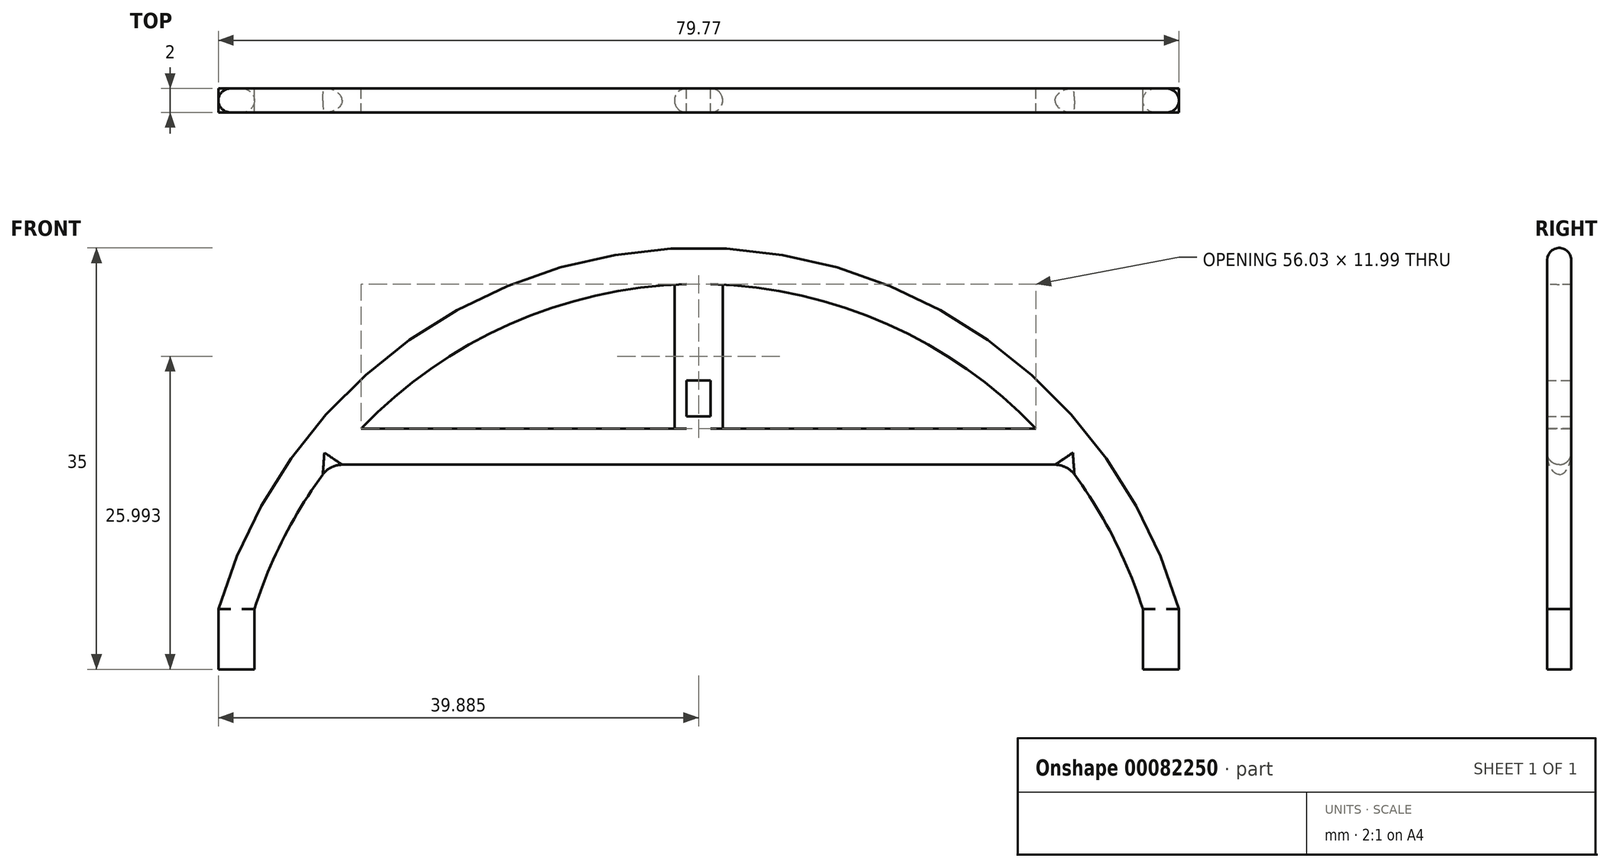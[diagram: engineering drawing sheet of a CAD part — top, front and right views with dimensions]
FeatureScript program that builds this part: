
annotation { "Feature Type Name" : "Feature", "Feature Type Description" : "" }
export const myFeature = defineFeature(function(context is Context, id is Id, definition is map)
    precondition{}
    {
        {
            var Q0;
            Q0=qCreatedBy(makeId("Front.planeOp"),FACE);
            var sketch = newSketch(context, id + "F0", { "sketchPlane" : qUnion([Q0])});
            skArc(sketch, "E0", {"start": v(34.32, -19.8) * mm, "mid": v(-5.57, 10.2) * mm, "end": v(-45.45, -19.8) * mm});
            skArc(sketch, "E1", {"start": v(31.32, -19.8) * mm, "mid": v(-5.57, 7.2) * mm, "end": v(-42.45, -19.8) * mm});
            skLineSegment(sketch, "E2", {"start": v(-45.45, -19.8) * mm, "end": v(-42.45, -19.8) * mm});
            skLineSegment(sketch, "E3", {"start": v(31.32, -19.8) * mm, "end": v(34.32, -19.8) * mm});
            skPoint(sketch, "E4.endSnap0", {"position": v(-5.57, 7.2) * mm});
            skLineSegment(sketch, "E5", {"start": v(-36.16, -7.8) * mm, "end": v(25.03, -7.8) * mm});
            skPoint(sketch, "E6.startSnap0", {"position": v(-5.57, -7.8) * mm});
            skLineSegment(sketch, "E7", {"start": v(-33.58, -4.8) * mm, "end": v(22.45, -4.8) * mm});
            skLineSegment(sketch, "E8", {"start": v(-7.57, 0.2) * mm, "end": v(-7.57, -4.8) * mm});
            skLineSegment(sketch, "E9", {"start": v(-3.57, 0.2) * mm, "end": v(-3.57, -4.8) * mm});
            skLineSegment(sketch, "E10", {"start": v(-6.57, -0.8) * mm, "end": v(-6.57, -3.8) * mm});
            skLineSegment(sketch, "E11", {"start": v(-6.57, -0.8) * mm, "end": v(-4.57, -0.8) * mm});
            skLineSegment(sketch, "E12", {"start": v(-4.57, -0.8) * mm, "end": v(-4.57, -3.8) * mm});
            skLineSegment(sketch, "E13", {"start": v(-4.57, -3.8) * mm, "end": v(-6.57, -3.8) * mm});
            skLineSegment(sketch, "E14", {"start": v(-7.57, 0.2) * mm, "end": v(-7.57, 7.15) * mm});
            skLineSegment(sketch, "E15", {"start": v(-3.57, 0.2) * mm, "end": v(-3.57, 7.15) * mm});
            skSolve(sketch);
        }
        {
            var Q0;
            Q0=makeQuery(id+"F0.imprint","IMPRINT",FACE,{"disambiguationData":[TD([[makeQuery(id+"F0.imprint","IMPRINT",EDGE,{"derivedFrom":sQuery(id+"F0.wireOp",EDGE,"E0")}),1.0]])]});
            var Q1;
            Q1=makeQuery(id+"F0.imprint","IMPRINT",FACE,{"disambiguationData":[TD([[makeQuery(id+"F0.imprint","IMPRINT",EDGE,{"derivedFrom":sQuery(id+"F0.wireOp",EDGE,"QaKfyl1q-dLBN-I6Pb-Zep1-DZlAWYqTSGp9")}),1.0]])]});
            var Q2;
            Q2=makeQuery(id+"F0.imprint","IMPRINT",FACE,{"disambiguationData":[TD([[makeQuery(id+"F0.imprint","IMPRINT",EDGE,{"derivedFrom":sQuery(id+"F0.wireOp",EDGE,"O7wW7FGu-E0O4-MFLM-AW0a-nUHi2M2s85NZ")}),-1.0]])]});
            var Q3;
            {var subQ0=sQuery(id+"F0.wireOp",EDGE,"E5");Q3=makeQuery(id+"F0.imprint","IMPRINT",FACE,{"disambiguationData":[TD([[makeQuery(id+"F0.imprint","IMPRINT",EDGE,{"derivedFrom":subQ0}),1.0]])]});}
            var Q4;
            {var subQ1=sQuery(id+"F0.wireOp",EDGE,"E8");Q4=makeQuery(id+"F0.imprint","IMPRINT",FACE,{"disambiguationData":[TD([[makeQuery(id+"F0.imprint","IMPRINT",EDGE,{"derivedFrom":subQ1}),1.0]])]});}
            extrude(context, id + "F1", {"entities" : qUnion([Q0, Q1, Q2, Q3, Q4]), "depth" : 2 * mm});
        }
        {
            var Q0;
            Q0=makeQuery(id+"F1.opExtrude","SWEPT_FACE",FACE,{"disambiguationData":[OSD([sQuery(id+"F0.wireOp",EDGE,"E3")])]});
            var sketch = newSketch(context, id + "F2", { "sketchPlane" : qUnion([Q0])});
            skLineSegment(sketch, "E16", {"start": v(31.32, 2) * mm, "end": v(31.32, 0) * mm});
            skLineSegment(sketch, "E17", {"start": v(31.32, 0) * mm, "end": v(34.32, 0) * mm});
            skLineSegment(sketch, "E18", {"start": v(34.32, 0) * mm, "end": v(34.32, 2) * mm});
            skLineSegment(sketch, "E19", {"start": v(34.32, 2) * mm, "end": v(31.32, 2) * mm});
            skSolve(sketch);
        }
        {
            var Q0;
            Q0=makeQuery(id+"F1.opExtrude","SWEPT_FACE",FACE,{"disambiguationData":[OSD([sQuery(id+"F0.wireOp",EDGE,"E2")])]});
            var sketch = newSketch(context, id + "F3", { "sketchPlane" : qUnion([Q0])});
            skLineSegment(sketch, "E20", {"start": v(-45.45, 2) * mm, "end": v(-45.45, 0) * mm});
            skLineSegment(sketch, "E21", {"start": v(-45.45, 0) * mm, "end": v(-42.45, 0) * mm});
            skLineSegment(sketch, "E22", {"start": v(-42.45, 0) * mm, "end": v(-42.45, 2) * mm});
            skLineSegment(sketch, "E23", {"start": v(-42.45, 2) * mm, "end": v(-45.45, 2) * mm});
            skSolve(sketch);
        }
        {
            var Q0;
            Q0=makeQuery(id+"F1.opExtrude","CAP_EDGE",EDGE,{"disambiguationData":[OSD([sQuery(id+"F0.wireOp",EDGE,"E0")])],"isStart":false});
            var Q1;
            {var subQ0=sQuery(id+"F0.wireOp",EDGE,"E1");Q1=makeQuery(id+"F1.opExtrude","CAP_EDGE",EDGE,{"disambiguationData":[OSD([subQ0]),TDD([makeQuery(id+"F0.imprint","IMPRINT",EDGE,{"disambiguationData":[TD([[makeQuery(id+"F0.imprint","INTERSECT",VERTEX,{"disambiguationData":[OD(0.0)],"derivedFrom":[subQ0,sQuery(id+"F0.wireOp",EDGE,"E7")]}),1.0]])],"derivedFrom":subQ0})])],"isStart":false});}
            var Q2;
            {var subQ0=sQuery(id+"F0.wireOp",EDGE,"E7");Q2=makeQuery(id+"F1.opExtrude","CAP_EDGE",EDGE,{"disambiguationData":[OSD([subQ0]),TDD([makeQuery(id+"F0.imprint","IMPRINT",EDGE,{"disambiguationData":[TD([[makeQuery(id+"F0.imprint","INTERSECT",VERTEX,{"disambiguationData":[OD(0.0)],"derivedFrom":[sQuery(id+"F0.wireOp",EDGE,"E1"),subQ0]}),-1.0]])],"derivedFrom":subQ0})])],"isStart":false});}
            var Q3;
            Q3=makeQuery(id+"F1.opExtrude","CAP_EDGE",EDGE,{"disambiguationData":[OSD([sQuery(id+"F0.wireOp",EDGE,"E8"),sQuery(id+"F0.wireOp",EDGE,"E14")])],"isStart":false});
            var Q4;
            Q4=makeQuery(id+"F1.opExtrude","CAP_EDGE",EDGE,{"disambiguationData":[OSD([sQuery(id+"F0.wireOp",EDGE,"E9"),sQuery(id+"F0.wireOp",EDGE,"E15")])],"isStart":false});
            var Q5;
            {var subQ0=sQuery(id+"F0.wireOp",EDGE,"E1");Q5=makeQuery(id+"F1.opExtrude","CAP_EDGE",EDGE,{"disambiguationData":[OSD([subQ0]),TDD([makeQuery(id+"F0.imprint","IMPRINT",EDGE,{"disambiguationData":[TD([[makeQuery(id+"F0.imprint","INTERSECT",VERTEX,{"disambiguationData":[OD(1.0)],"derivedFrom":[subQ0,sQuery(id+"F0.wireOp",EDGE,"E7")]}),-1.0]])],"derivedFrom":subQ0})])],"isStart":false});}
            var Q6;
            {var subQ0=sQuery(id+"F0.wireOp",EDGE,"E7");Q6=makeQuery(id+"F1.opExtrude","CAP_EDGE",EDGE,{"disambiguationData":[OSD([subQ0]),TDD([makeQuery(id+"F0.imprint","IMPRINT",EDGE,{"disambiguationData":[TD([[makeQuery(id+"F0.imprint","INTERSECT",VERTEX,{"disambiguationData":[OD(1.0)],"derivedFrom":[sQuery(id+"F0.wireOp",EDGE,"E1"),subQ0]}),1.0]])],"derivedFrom":subQ0})])],"isStart":false});}
            var Q7;
            Q7=makeQuery(id+"F1.opExtrude","CAP_EDGE",EDGE,{"disambiguationData":[OSD([sQuery(id+"F0.wireOp",EDGE,"E0")])],"isStart":true});
            var Q8;
            {var subQ0=sQuery(id+"F0.wireOp",EDGE,"E7");Q8=makeQuery(id+"F1.opExtrude","CAP_EDGE",EDGE,{"disambiguationData":[OSD([subQ0]),TDD([makeQuery(id+"F0.imprint","IMPRINT",EDGE,{"disambiguationData":[TD([[makeQuery(id+"F0.imprint","INTERSECT",VERTEX,{"disambiguationData":[OD(1.0)],"derivedFrom":[sQuery(id+"F0.wireOp",EDGE,"E1"),subQ0]}),1.0]])],"derivedFrom":subQ0})])],"isStart":true});}
            var Q9;
            {var subQ0=sQuery(id+"F0.wireOp",EDGE,"E1");Q9=makeQuery(id+"F1.opExtrude","CAP_EDGE",EDGE,{"disambiguationData":[OSD([subQ0]),TDD([makeQuery(id+"F0.imprint","IMPRINT",EDGE,{"disambiguationData":[TD([[makeQuery(id+"F0.imprint","INTERSECT",VERTEX,{"disambiguationData":[OD(1.0)],"derivedFrom":[subQ0,sQuery(id+"F0.wireOp",EDGE,"E7")]}),-1.0]])],"derivedFrom":subQ0})])],"isStart":true});}
            var Q10;
            Q10=makeQuery(id+"F1.opExtrude","CAP_EDGE",EDGE,{"disambiguationData":[OSD([sQuery(id+"F0.wireOp",EDGE,"E9"),sQuery(id+"F0.wireOp",EDGE,"E15")])],"isStart":true});
            var Q11;
            {var subQ0=sQuery(id+"F0.wireOp",EDGE,"E1");Q11=makeQuery(id+"F1.opExtrude","CAP_EDGE",EDGE,{"disambiguationData":[OSD([subQ0]),TDD([makeQuery(id+"F0.imprint","IMPRINT",EDGE,{"disambiguationData":[TD([[makeQuery(id+"F0.imprint","INTERSECT",VERTEX,{"disambiguationData":[OD(0.0)],"derivedFrom":[subQ0,sQuery(id+"F0.wireOp",EDGE,"E7")]}),1.0]])],"derivedFrom":subQ0})])],"isStart":true});}
            var Q12;
            Q12=makeQuery(id+"F1.opExtrude","CAP_EDGE",EDGE,{"disambiguationData":[OSD([sQuery(id+"F0.wireOp",EDGE,"E8"),sQuery(id+"F0.wireOp",EDGE,"E14")])],"isStart":true});
            var Q13;
            {var subQ0=sQuery(id+"F0.wireOp",EDGE,"E7");Q13=makeQuery(id+"F1.opExtrude","CAP_EDGE",EDGE,{"disambiguationData":[OSD([subQ0]),TDD([makeQuery(id+"F0.imprint","IMPRINT",EDGE,{"disambiguationData":[TD([[makeQuery(id+"F0.imprint","INTERSECT",VERTEX,{"disambiguationData":[OD(0.0)],"derivedFrom":[sQuery(id+"F0.wireOp",EDGE,"E1"),subQ0]}),-1.0]])],"derivedFrom":subQ0})])],"isStart":true});}
            var Q14;
            {var subQ0=sQuery(id+"F0.wireOp",EDGE,"E1");Q14=makeQuery(id+"F1.opExtrude","CAP_EDGE",EDGE,{"disambiguationData":[OSD([subQ0]),TDD([makeQuery(id+"F0.imprint","IMPRINT",EDGE,{"disambiguationData":[TD([[makeQuery(id+"F0.imprint","INTERSECT",VERTEX,{"disambiguationData":[OD(0.0)],"derivedFrom":[subQ0,sQuery(id+"F0.wireOp",EDGE,"E5")]}),-1.0]])],"derivedFrom":subQ0})])],"isStart":true});}
            var Q15;
            {var subQ0=sQuery(id+"F0.wireOp",EDGE,"E1");Q15=makeQuery(id+"F1.opExtrude","CAP_EDGE",EDGE,{"disambiguationData":[OSD([subQ0]),TDD([makeQuery(id+"F0.imprint","IMPRINT",EDGE,{"disambiguationData":[TD([[makeQuery(id+"F0.imprint","INTERSECT",VERTEX,{"disambiguationData":[OD(1.0)],"derivedFrom":[subQ0,sQuery(id+"F0.wireOp",EDGE,"E5")]}),1.0]])],"derivedFrom":subQ0})])],"isStart":true});}
            var Q16;
            Q16=makeQuery(id+"F1.opExtrude","CAP_EDGE",EDGE,{"disambiguationData":[OSD([sQuery(id+"F0.wireOp",EDGE,"E5")])],"isStart":true});
            var Q17;
            {var subQ0=sQuery(id+"F0.wireOp",EDGE,"E1");Q17=makeQuery(id+"F1.opExtrude","CAP_EDGE",EDGE,{"disambiguationData":[OSD([subQ0]),TDD([makeQuery(id+"F0.imprint","IMPRINT",EDGE,{"disambiguationData":[TD([[makeQuery(id+"F0.imprint","INTERSECT",VERTEX,{"disambiguationData":[OD(0.0)],"derivedFrom":[subQ0,sQuery(id+"F0.wireOp",EDGE,"E5")]}),-1.0]])],"derivedFrom":subQ0})])],"isStart":false});}
            var Q18;
            Q18=makeQuery(id+"F1.opExtrude","CAP_EDGE",EDGE,{"disambiguationData":[OSD([sQuery(id+"F0.wireOp",EDGE,"E5")])],"isStart":false});
            var Q19;
            {var subQ0=sQuery(id+"F0.wireOp",EDGE,"E1");Q19=makeQuery(id+"F1.opExtrude","CAP_EDGE",EDGE,{"disambiguationData":[OSD([subQ0]),TDD([makeQuery(id+"F0.imprint","IMPRINT",EDGE,{"disambiguationData":[TD([[makeQuery(id+"F0.imprint","INTERSECT",VERTEX,{"disambiguationData":[OD(1.0)],"derivedFrom":[subQ0,sQuery(id+"F0.wireOp",EDGE,"E5")]}),1.0]])],"derivedFrom":subQ0})])],"isStart":false});}
            fillet(context, id + "F4", {"entities" : qUnion([Q0, Q1, Q2, Q3, Q4, Q5, Q6, Q7, Q8, Q9, Q10, Q11, Q12, Q13, Q14, Q15, Q16, Q17, Q18, Q19]), "radius" : 1 * mm, "tangentPropagation" : true, "allowEdgeOverflow" : false});
        }
        {
            var Q0;
            {var subQ0=sQuery(id+"F0.wireOp",EDGE,"E7");var subQ1=sQuery(id+"F0.wireOp",EDGE,"E1");var subQ2=makeQuery(id+"F0.imprint","INTERSECT",VERTEX,{"disambiguationData":[OD(0.0)],"derivedFrom":[subQ1,subQ0]});Q0=makeQuery(id+"F4.opFillet","BLEND_EDGE",EDGE,{"blendedFrom":[makeQuery(id+"F1.opExtrude","CAP_EDGE",EDGE,{"disambiguationData":[OSD([subQ1]),TDD([makeQuery(id+"F0.imprint","IMPRINT",EDGE,{"disambiguationData":[TD([[subQ2,1.0]])],"derivedFrom":subQ1})])],"isStart":false}),makeQuery(id+"F1.opExtrude","CAP_EDGE",EDGE,{"disambiguationData":[OSD([subQ0]),TDD([makeQuery(id+"F0.imprint","IMPRINT",EDGE,{"disambiguationData":[TD([[subQ2,-1.0]])],"derivedFrom":subQ0})])],"isStart":false})],"blendedInto":[]});}
            var Q1;
            {var subQ0=sQuery(id+"F0.wireOp",EDGE,"E7");var subQ1=sQuery(id+"F0.wireOp",EDGE,"E1");var subQ2=makeQuery(id+"F0.imprint","INTERSECT",VERTEX,{"disambiguationData":[OD(0.0)],"derivedFrom":[subQ1,subQ0]});Q1=makeQuery(id+"F4.opFillet","BLEND_EDGE",EDGE,{"blendedFrom":[makeQuery(id+"F1.opExtrude","CAP_EDGE",EDGE,{"disambiguationData":[OSD([subQ1]),TDD([makeQuery(id+"F0.imprint","IMPRINT",EDGE,{"disambiguationData":[TD([[subQ2,1.0]])],"derivedFrom":subQ1})])],"isStart":true}),makeQuery(id+"F1.opExtrude","CAP_EDGE",EDGE,{"disambiguationData":[OSD([subQ0]),TDD([makeQuery(id+"F0.imprint","IMPRINT",EDGE,{"disambiguationData":[TD([[subQ2,-1.0]])],"derivedFrom":subQ0})])],"isStart":true})],"blendedInto":[]});}
            var Q2;
            {var subQ0=sQuery(id+"F0.wireOp",EDGE,"E7");var subQ1=sQuery(id+"F0.wireOp",EDGE,"E1");var subQ2=makeQuery(id+"F0.imprint","INTERSECT",VERTEX,{"disambiguationData":[OD(1.0)],"derivedFrom":[subQ1,subQ0]});Q2=makeQuery(id+"F4.opFillet","BLEND_EDGE",EDGE,{"blendedFrom":[makeQuery(id+"F1.opExtrude","CAP_EDGE",EDGE,{"disambiguationData":[OSD([subQ1]),TDD([makeQuery(id+"F0.imprint","IMPRINT",EDGE,{"disambiguationData":[TD([[subQ2,-1.0]])],"derivedFrom":subQ1})])],"isStart":true}),makeQuery(id+"F1.opExtrude","CAP_EDGE",EDGE,{"disambiguationData":[OSD([subQ0]),TDD([makeQuery(id+"F0.imprint","IMPRINT",EDGE,{"disambiguationData":[TD([[subQ2,1.0]])],"derivedFrom":subQ0})])],"isStart":true})],"blendedInto":[]});}
            var Q3;
            {var subQ0=sQuery(id+"F0.wireOp",EDGE,"E7");var subQ1=sQuery(id+"F0.wireOp",EDGE,"E1");var subQ2=makeQuery(id+"F0.imprint","INTERSECT",VERTEX,{"disambiguationData":[OD(1.0)],"derivedFrom":[subQ1,subQ0]});Q3=makeQuery(id+"F4.opFillet","BLEND_EDGE",EDGE,{"blendedFrom":[makeQuery(id+"F1.opExtrude","CAP_EDGE",EDGE,{"disambiguationData":[OSD([subQ1]),TDD([makeQuery(id+"F0.imprint","IMPRINT",EDGE,{"disambiguationData":[TD([[subQ2,-1.0]])],"derivedFrom":subQ1})])],"isStart":false}),makeQuery(id+"F1.opExtrude","CAP_EDGE",EDGE,{"disambiguationData":[OSD([subQ0]),TDD([makeQuery(id+"F0.imprint","IMPRINT",EDGE,{"disambiguationData":[TD([[subQ2,1.0]])],"derivedFrom":subQ0})])],"isStart":false})],"blendedInto":[]});}
            var Q4;
            {var subQ0=sQuery(id+"F0.wireOp",EDGE,"E8");var subQ1=sQuery(id+"F0.wireOp",EDGE,"E7");Q4=makeQuery(id+"F4.opFillet","BLEND_EDGE",EDGE,{"blendedFrom":[makeQuery(id+"F1.opExtrude","CAP_EDGE",EDGE,{"disambiguationData":[OSD([subQ1]),TDD([makeQuery(id+"F0.imprint","IMPRINT",EDGE,{"disambiguationData":[TD([[makeQuery(id+"F0.imprint","INTERSECT",VERTEX,{"disambiguationData":[OD(0.0)],"derivedFrom":[sQuery(id+"F0.wireOp",EDGE,"E1"),subQ1]}),-1.0]])],"derivedFrom":subQ1})])],"isStart":false}),makeQuery(id+"F1.opExtrude","CAP_EDGE",EDGE,{"disambiguationData":[OSD([subQ0,sQuery(id+"F0.wireOp",EDGE,"E14")])],"isStart":false})],"blendedInto":[]});}
            var Q5;
            {var subQ0=sQuery(id+"F0.wireOp",EDGE,"E9");var subQ1=sQuery(id+"F0.wireOp",EDGE,"E7");Q5=makeQuery(id+"F4.opFillet","BLEND_EDGE",EDGE,{"blendedFrom":[makeQuery(id+"F1.opExtrude","CAP_EDGE",EDGE,{"disambiguationData":[OSD([subQ1]),TDD([makeQuery(id+"F0.imprint","IMPRINT",EDGE,{"disambiguationData":[TD([[makeQuery(id+"F0.imprint","INTERSECT",VERTEX,{"disambiguationData":[OD(1.0)],"derivedFrom":[sQuery(id+"F0.wireOp",EDGE,"E1"),subQ1]}),1.0]])],"derivedFrom":subQ1})])],"isStart":false}),makeQuery(id+"F1.opExtrude","CAP_EDGE",EDGE,{"disambiguationData":[OSD([subQ0,sQuery(id+"F0.wireOp",EDGE,"E15")])],"isStart":false})],"blendedInto":[]});}
            var Q6;
            {var subQ0=sQuery(id+"F0.wireOp",EDGE,"E15");var subQ1=sQuery(id+"F0.wireOp",EDGE,"E1");Q6=makeQuery(id+"F4.opFillet","BLEND_EDGE",EDGE,{"blendedFrom":[makeQuery(id+"F1.opExtrude","CAP_EDGE",EDGE,{"disambiguationData":[OSD([subQ1]),TDD([makeQuery(id+"F0.imprint","IMPRINT",EDGE,{"disambiguationData":[TD([[makeQuery(id+"F0.imprint","INTERSECT",VERTEX,{"disambiguationData":[OD(1.0)],"derivedFrom":[subQ1,sQuery(id+"F0.wireOp",EDGE,"E7")]}),-1.0]])],"derivedFrom":subQ1})])],"isStart":false}),makeQuery(id+"F1.opExtrude","CAP_EDGE",EDGE,{"disambiguationData":[OSD([sQuery(id+"F0.wireOp",EDGE,"E9"),subQ0])],"isStart":false})],"blendedInto":[]});}
            var Q7;
            {var subQ0=sQuery(id+"F0.wireOp",EDGE,"E15");var subQ1=sQuery(id+"F0.wireOp",EDGE,"E1");Q7=makeQuery(id+"F4.opFillet","BLEND_EDGE",EDGE,{"blendedFrom":[makeQuery(id+"F1.opExtrude","CAP_EDGE",EDGE,{"disambiguationData":[OSD([subQ1]),TDD([makeQuery(id+"F0.imprint","IMPRINT",EDGE,{"disambiguationData":[TD([[makeQuery(id+"F0.imprint","INTERSECT",VERTEX,{"disambiguationData":[OD(1.0)],"derivedFrom":[subQ1,sQuery(id+"F0.wireOp",EDGE,"E7")]}),-1.0]])],"derivedFrom":subQ1})])],"isStart":true}),makeQuery(id+"F1.opExtrude","CAP_EDGE",EDGE,{"disambiguationData":[OSD([sQuery(id+"F0.wireOp",EDGE,"E9"),subQ0])],"isStart":true})],"blendedInto":[]});}
            var Q8;
            {var subQ0=sQuery(id+"F0.wireOp",EDGE,"E14");var subQ1=sQuery(id+"F0.wireOp",EDGE,"E1");Q8=makeQuery(id+"F4.opFillet","BLEND_EDGE",EDGE,{"blendedFrom":[makeQuery(id+"F1.opExtrude","CAP_EDGE",EDGE,{"disambiguationData":[OSD([subQ1]),TDD([makeQuery(id+"F0.imprint","IMPRINT",EDGE,{"disambiguationData":[TD([[makeQuery(id+"F0.imprint","INTERSECT",VERTEX,{"disambiguationData":[OD(0.0)],"derivedFrom":[subQ1,sQuery(id+"F0.wireOp",EDGE,"E7")]}),1.0]])],"derivedFrom":subQ1})])],"isStart":true}),makeQuery(id+"F1.opExtrude","CAP_EDGE",EDGE,{"disambiguationData":[OSD([sQuery(id+"F0.wireOp",EDGE,"E8"),subQ0])],"isStart":true})],"blendedInto":[]});}
            var Q9;
            {var subQ0=sQuery(id+"F0.wireOp",EDGE,"E14");var subQ1=sQuery(id+"F0.wireOp",EDGE,"E1");Q9=makeQuery(id+"F4.opFillet","BLEND_EDGE",EDGE,{"blendedFrom":[makeQuery(id+"F1.opExtrude","CAP_EDGE",EDGE,{"disambiguationData":[OSD([subQ1]),TDD([makeQuery(id+"F0.imprint","IMPRINT",EDGE,{"disambiguationData":[TD([[makeQuery(id+"F0.imprint","INTERSECT",VERTEX,{"disambiguationData":[OD(0.0)],"derivedFrom":[subQ1,sQuery(id+"F0.wireOp",EDGE,"E7")]}),1.0]])],"derivedFrom":subQ1})])],"isStart":false}),makeQuery(id+"F1.opExtrude","CAP_EDGE",EDGE,{"disambiguationData":[OSD([sQuery(id+"F0.wireOp",EDGE,"E8"),subQ0])],"isStart":false})],"blendedInto":[]});}
            var Q10;
            {var subQ0=sQuery(id+"F0.wireOp",EDGE,"E5");var subQ1=sQuery(id+"F0.wireOp",EDGE,"E1");Q10=makeQuery(id+"F4.opFillet","BLEND_EDGE",EDGE,{"blendedFrom":[makeQuery(id+"F1.opExtrude","CAP_EDGE",EDGE,{"disambiguationData":[OSD([subQ1]),TDD([makeQuery(id+"F0.imprint","IMPRINT",EDGE,{"disambiguationData":[TD([[makeQuery(id+"F0.imprint","INTERSECT",VERTEX,{"derivedFrom":[subQ1,sQuery(id+"F0.wireOp",EDGE,"E2")]}),1.0]])],"derivedFrom":subQ1})])],"isStart":false}),makeQuery(id+"F1.opExtrude","CAP_EDGE",EDGE,{"disambiguationData":[OSD([subQ0])],"isStart":false})],"blendedInto":[]});}
            var Q11;
            {var subQ0=sQuery(id+"F0.wireOp",EDGE,"E5");var subQ1=sQuery(id+"F0.wireOp",EDGE,"E1");Q11=makeQuery(id+"F4.opFillet","BLEND_EDGE",EDGE,{"blendedFrom":[makeQuery(id+"F1.opExtrude","CAP_EDGE",EDGE,{"disambiguationData":[OSD([subQ1]),TDD([makeQuery(id+"F0.imprint","IMPRINT",EDGE,{"disambiguationData":[TD([[makeQuery(id+"F0.imprint","INTERSECT",VERTEX,{"derivedFrom":[subQ1,sQuery(id+"F0.wireOp",EDGE,"E2")]}),1.0]])],"derivedFrom":subQ1})])],"isStart":true}),makeQuery(id+"F1.opExtrude","CAP_EDGE",EDGE,{"disambiguationData":[OSD([subQ0])],"isStart":true})],"blendedInto":[]});}
            var Q12;
            {var subQ0=sQuery(id+"F0.wireOp",EDGE,"E5");var subQ1=sQuery(id+"F0.wireOp",EDGE,"E1");Q12=makeQuery(id+"F4.opFillet","BLEND_EDGE",EDGE,{"blendedFrom":[makeQuery(id+"F1.opExtrude","CAP_EDGE",EDGE,{"disambiguationData":[OSD([subQ1]),TDD([makeQuery(id+"F0.imprint","IMPRINT",EDGE,{"disambiguationData":[TD([[makeQuery(id+"F0.imprint","INTERSECT",VERTEX,{"derivedFrom":[subQ1,sQuery(id+"F0.wireOp",EDGE,"E3")]}),-1.0]])],"derivedFrom":subQ1})])],"isStart":true}),makeQuery(id+"F1.opExtrude","CAP_EDGE",EDGE,{"disambiguationData":[OSD([subQ0])],"isStart":true})],"blendedInto":[]});}
            var Q13;
            {var subQ0=sQuery(id+"F0.wireOp",EDGE,"E5");var subQ1=sQuery(id+"F0.wireOp",EDGE,"E1");Q13=makeQuery(id+"F4.opFillet","BLEND_EDGE",EDGE,{"blendedFrom":[makeQuery(id+"F1.opExtrude","CAP_EDGE",EDGE,{"disambiguationData":[OSD([subQ1]),TDD([makeQuery(id+"F0.imprint","IMPRINT",EDGE,{"disambiguationData":[TD([[makeQuery(id+"F0.imprint","INTERSECT",VERTEX,{"derivedFrom":[subQ1,sQuery(id+"F0.wireOp",EDGE,"E3")]}),-1.0]])],"derivedFrom":subQ1})])],"isStart":false}),makeQuery(id+"F1.opExtrude","CAP_EDGE",EDGE,{"disambiguationData":[OSD([subQ0])],"isStart":false})],"blendedInto":[]});}
            fillet(context, id + "F5", {"entities" : qUnion([Q0, Q1, Q2, Q3, Q4, Q5, Q6, Q7, Q8, Q9, Q10, Q11, Q12, Q13]), "radius" : 2 * mm, "tangentPropagation" : true, "allowEdgeOverflow" : false});
        }
        {
            var Q0;
            Q0=makeQuery(id+"F3.imprint","IMPRINT",FACE,{"disambiguationData":[TD([[makeQuery(id+"F3.imprint","IMPRINT",EDGE,{"derivedFrom":sQuery(id+"F3.wireOp",EDGE,"E20")}),1.0]])]});
            extrude(context, id + "F6", {"entities" : qUnion([Q0]), "operationType" : NewBodyOperationType.ADD, "depth" : 5 * mm});
        }
        {
            var Q0;
            Q0=makeQuery(id+"F2.imprint","IMPRINT",FACE,{"disambiguationData":[TD([[makeQuery(id+"F2.imprint","IMPRINT",EDGE,{"derivedFrom":sQuery(id+"F2.wireOp",EDGE,"E16")}),1.0]])]});
            extrude(context, id + "F7", {"entities" : qUnion([Q0]), "operationType" : NewBodyOperationType.ADD, "depth" : 5 * mm});
        }
    });
